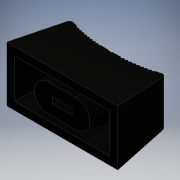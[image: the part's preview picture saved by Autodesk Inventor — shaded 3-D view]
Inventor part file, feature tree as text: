
AUTODESK INVENTOR PART (.ipt)
format: ipt  version: 2016 SP2 (Build 200236200, 236)  size: 366,080 bytes
history: native  units: mm
features: extrude x6, sketch x6, mirror x2, other x1, fillet x1, pattern_circular x1, projected_geometry x1
ambient origin geometry x8: Origin, YZ Plane, XZ Plane, XY Plane, X Axis, Y Axis, Z Axis, Center Point
bodies: Body1 (feature_tree)
feature tree (18):
  other  "Bryła1"
  extrude  "Wyciągnięcie proste1"  Depth=3.0734mm
  extrude  "Wyciągnięcie proste2"  Depth=3.9878mm
  extrude  "Wyciągnięcie proste3"  Depth=7.9248mm
  fillet  "Zaokrąglenie1"  Radius=0.635mm
  pattern_circular  "Szyk kołowy1"  [2 undecoded]
  mirror  "Odbicie lustrzane1"
  mirror  "Odbicie lustrzane2"
  extrude  "Wyciągnięcie proste4"  Depth=22.225mm
  extrude  "Wyciągnięcie proste5"  Depth=11.0998mm
  extrude  "Wyciągnięcie proste6"  Depth=1.396263mm
  sketch  "Szkic1"
  sketch  "Szkic2"
  sketch  "Szkic3"
  sketch  "Szkic4"
  sketch  "Szkic5"
  sketch  "Szkic6"
  projected_geometry  "Pętla rzutowana1"
note: 2 required parameter values undecoded (feature->parameter linkage not recoverable at this tier; creation-order binding heuristic only, values carry confidence <= 0.55)
